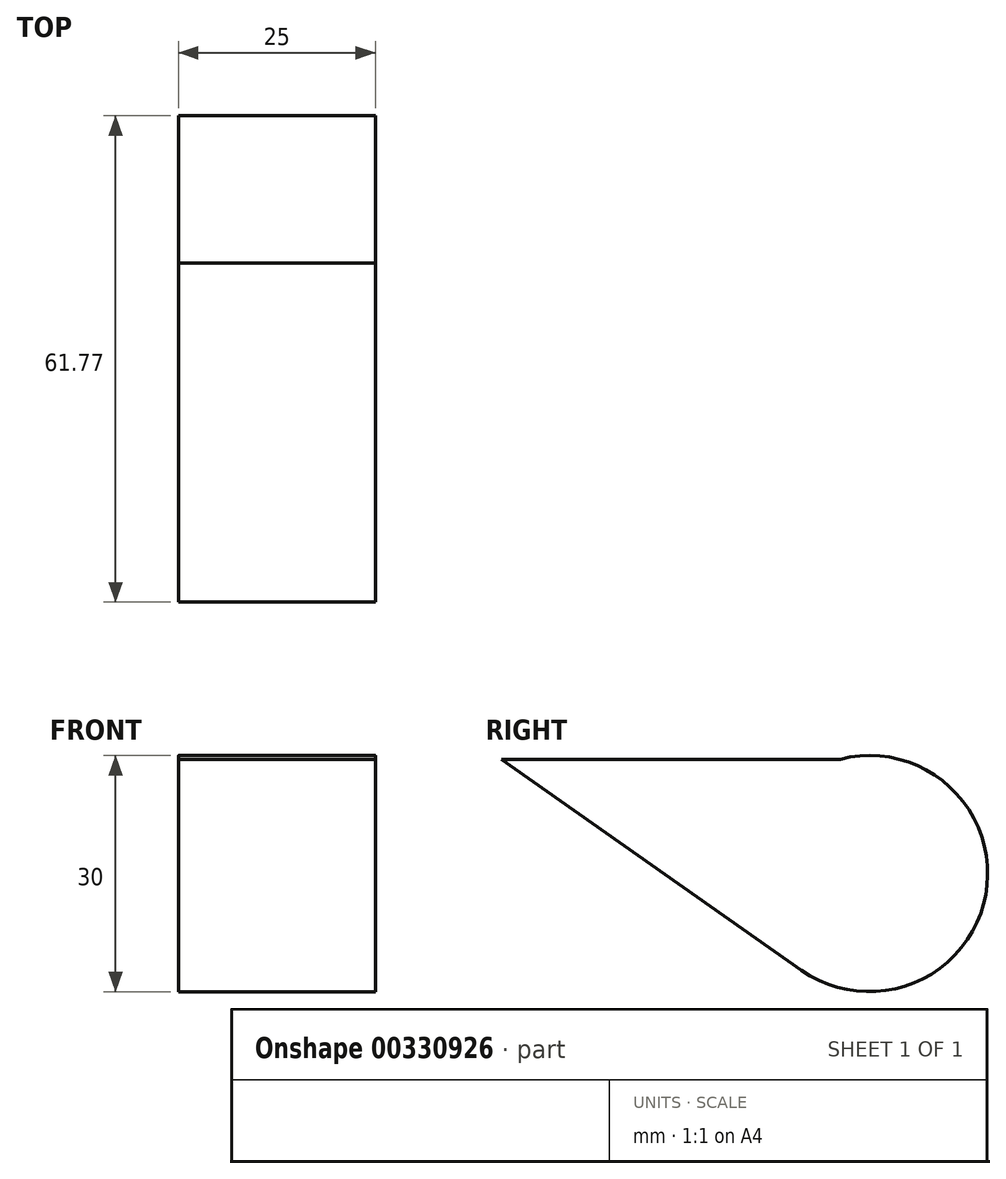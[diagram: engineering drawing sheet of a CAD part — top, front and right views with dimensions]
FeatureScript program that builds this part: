
annotation { "Feature Type Name" : "Feature", "Feature Type Description" : "" }
export const myFeature = defineFeature(function(context is Context, id is Id, definition is map)
    precondition{}
    {
        {
            var Q0;
            Q0=qCreatedBy(makeId("Right.planeOp"),FACE);
            var sketch = newSketch(context, id + "F0", { "sketchPlane" : qUnion([Q0])});
            skArc(sketch, "E0", {"start": v(-16.53, 1.62) * mm, "mid": v(6.85, 11.2) * mm, "end": v(-11.64, 28.42) * mm});
            skLineSegment(sketch, "E1", {"start": v(-11.64, 28.42) * mm, "end": v(-54.68, 28.42) * mm});
            skLineSegment(sketch, "E2", {"start": v(-54.68, 28.42) * mm, "end": v(-16.53, 1.62) * mm});
            skSolve(sketch);
        }
        {
            var Q0;
            Q0 = qSketchRegion(id + "F0", true);
            extrude(context, id + "F1", {"entities" : qUnion([Q0]), "depth" : 25 * mm});
        }
    });
